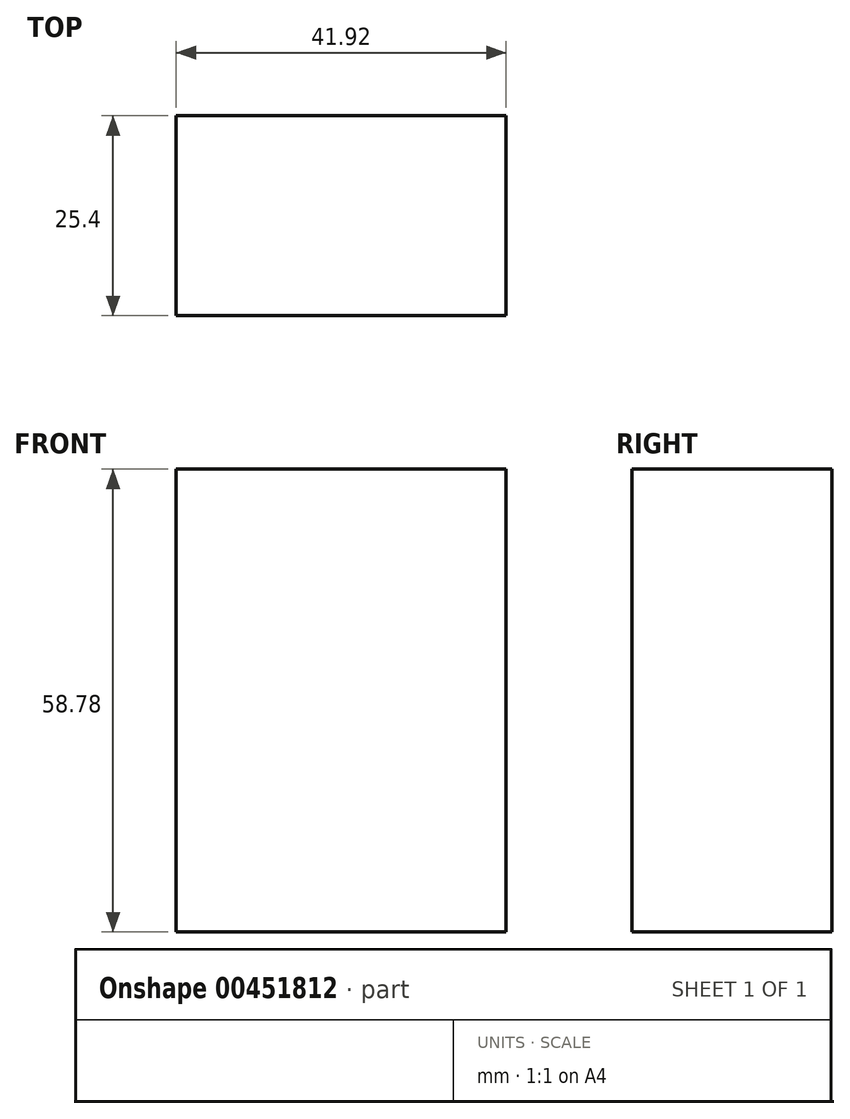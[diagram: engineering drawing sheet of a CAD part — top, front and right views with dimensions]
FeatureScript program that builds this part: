
annotation { "Feature Type Name" : "Feature", "Feature Type Description" : "" }
export const myFeature = defineFeature(function(context is Context, id is Id, definition is map)
    precondition{}
    {
        {
            var Q0;
            Q0=qCreatedBy(makeId("Front.planeOp"),FACE);
            var sketch = newSketch(context, id + "F0", { "sketchPlane" : qUnion([Q0])});
            skLineSegment(sketch, "E0.bottom", {"start": v(20.95, -46.99) * mm, "end": v(-20.95, -46.99) * mm});
            skLineSegment(sketch, "E0.top", {"start": v(20.95, 11.79) * mm, "end": v(-20.95, 11.79) * mm});
            skLineSegment(sketch, "E0.left", {"start": v(20.96, -46.99) * mm, "end": v(20.95, 11.79) * mm});
            skLineSegment(sketch, "E0.right", {"start": v(-20.96, -46.99) * mm, "end": v(-20.96, 11.79) * mm});
            skPoint(sketch, "E0.middle", {"position": v(0, -17.6) * mm});
            skArc(sketch, "E1", {"start": v(20.95, 11.79) * mm, "mid": v(17.6, 23.15) * mm, "end": v(8.62, 30.89) * mm});
            skFitSpline(sketch, "E2", {"points": [v(-8.62, 30.89) * mm, v(-4.43, 35.78) * mm, v(-3.4, 40.55) * mm], "startDerivative": vector(9.36, 8.83) * mm, "endDerivative": vector(0.88, 10.51) * mm});
            skFitSpline(sketch, "E3", {"points": [v(8.62, 30.89) * mm, v(5.45, 35.78) * mm, v(4.77, 40.55) * mm], "startDerivative": vector(-7.26, 9.17) * mm, "endDerivative": vector(-0.33, 10.18) * mm});
            skArc(sketch, "E4.trimOffspring", {"start": v(-8.62, 30.89) * mm, "mid": v(-17.6, 23.15) * mm, "end": v(-20.95, 11.79) * mm});
            skSolve(sketch);
        }
        {
            var Q0;
            Q0 = qSketchRegion(id + "F0", true);
            extrude(context, id + "F1", {"entities" : qUnion([Q0]), "depth" : 25.4 * mm});
        }
    });
